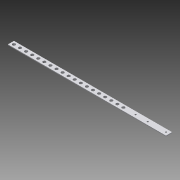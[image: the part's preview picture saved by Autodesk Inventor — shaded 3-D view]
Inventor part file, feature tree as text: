
AUTODESK INVENTOR PART (.ipt)
format: ipt  version: 2015 (Build 190159000, 159)  size: 151,040 bytes
history: native  units: in
note: dims shown in document units (in); Inventor stores cm internally (conversion verified against a paired STEP export)
features: sketch x5, projected_geometry x4, extrude x3, hole x2, pattern_linear x1
ambient origin geometry x8: Origin, YZ Plane, XZ Plane, XY Plane, X Axis, Y Axis, Z Axis, Center Point
bodies: Solid1 (feature_tree)
feature tree (15):
  extrude  "Extrusion1"  Depth=1.0in
  extrude  "Extrusion2"  Depth=0.125in
  sketch  "Sketch3"  dims[d4=26.0in d5=0.0in d6=6.5in]
  extrude  "Extrusion3"  Depth=6.5in
  hole  "Hole2"  [1 undecoded]
  pattern_linear  "Rectangular Pattern1"  Spacing1=0.5in  [1 undecoded]
  hole  "Hole3"  [1 undecoded]
  sketch  "Sketch1"  dims[d0=0.125in d1=1.0in]
  sketch  "Sketch2"  dims[d2=1.0in d3=0.125in]
  projected_geometry  "Projected Loop1"
  projected_geometry  "Projected Loop2"
  sketch  "Sketch4"  dims[d7=0.875in d8=1.0in d9=0.0in]
  projected_geometry  "Projected Loop3"
  sketch  "Sketch5"  dims[d10=0.5in d11=0.5in d12=5.5in d13=0.5in d21=19.5in d22=0.5in d23=1.0in d24=0.0in d25=0.5in d26=0.5in d27=0.5in d28=0.75in d29=0.375in d30=0.25in d31=0.5635in d32=1.0in d33=0.8108in d34=7.4803in d36=1.0in d37=3.5in d38=0.5in d39=0.2656in d40=0.75in d41=0.375in d42=0.25in d43=0.5635in d44=1.0in d45=0.8108in]
  projected_geometry  "Projected Loop4"
note: 3 required parameter values undecoded (feature->parameter linkage not recoverable at this tier; creation-order binding heuristic only, values carry confidence <= 0.55)
